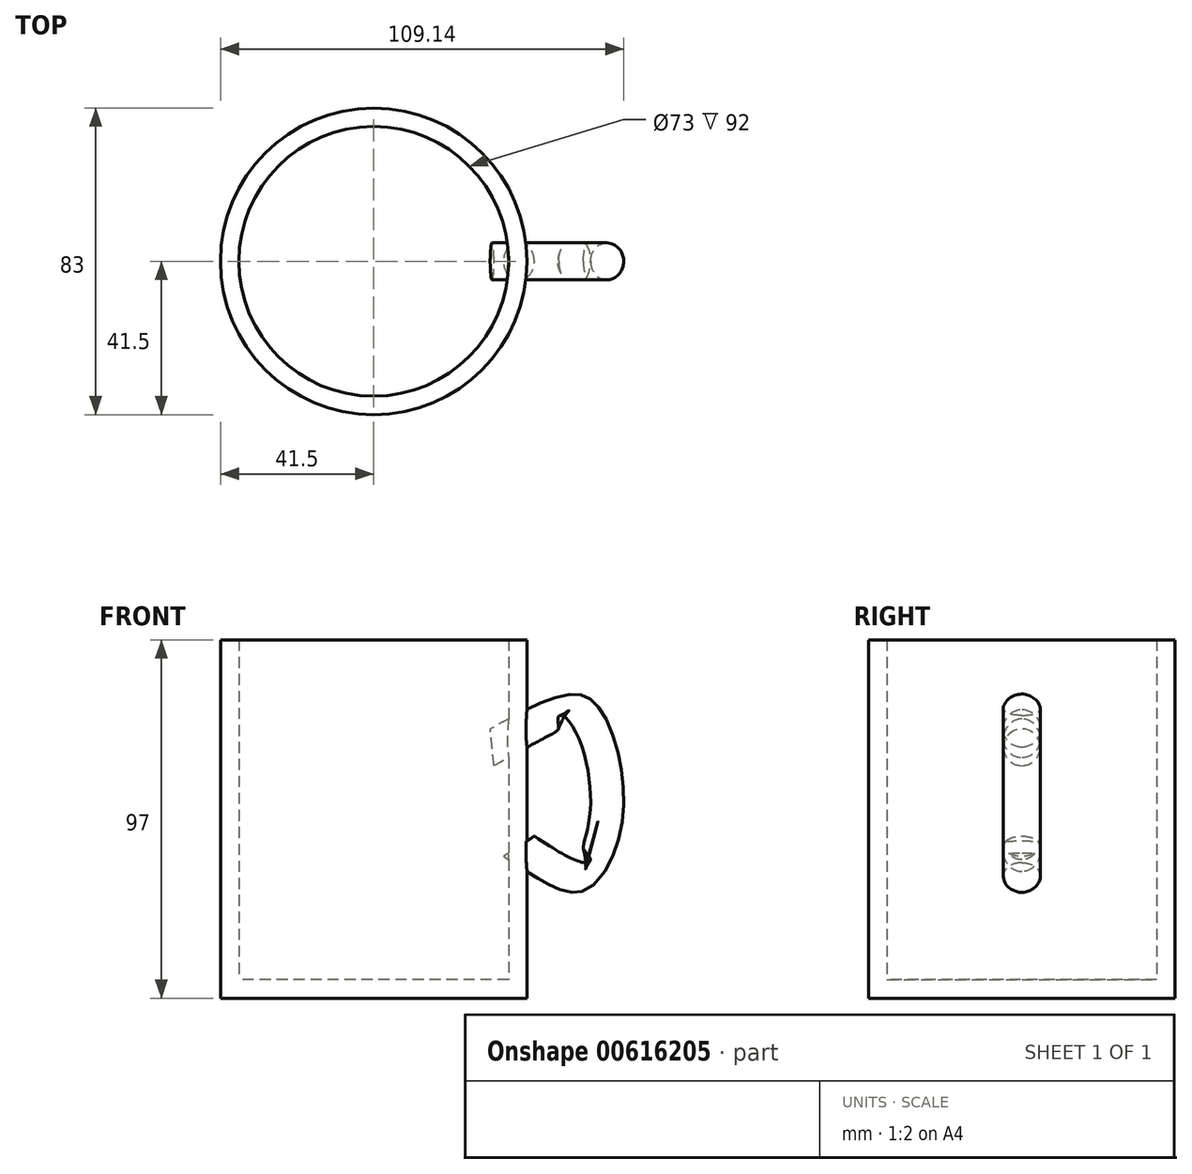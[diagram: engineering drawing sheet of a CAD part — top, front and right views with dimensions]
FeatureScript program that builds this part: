
annotation { "Feature Type Name" : "Feature", "Feature Type Description" : "" }
export const myFeature = defineFeature(function(context is Context, id is Id, definition is map)
    precondition{}
    {
        {
            var Q0;
            Q0=qCreatedBy(makeId("Top.planeOp"),FACE);
            var sketch = newSketch(context, id + "F0", { "sketchPlane" : qUnion([Q0])});
            skCircle(sketch, "E0", {"center": v(0, 0) * mm, "radius": 41.5 * mm});
            skSolve(sketch);
        }
        {
            var Q0;
            Q0 = qSketchRegion(id + "F0", true);
            extrude(context, id + "F1", {"entities" : qUnion([Q0]), "depth" : 97 * mm, "offsetDistance" : 25 * mm});
        }
        {
            var Q0;
            Q0=makeQuery(id+"F1.opExtrude","CAP_FACE",FACE,{"disambiguationData":[OSD([sQuery(id+"F0.wireOp",EDGE,"E0")])],"isStart":false});
            shell(context, id + "F2", {"entities" : qUnion([Q0]), "thickness" : 5 * mm});
        }
        {
            var Q0;
            Q0=qCreatedBy(makeId("Front.planeOp"),FACE);
            var sketch = newSketch(context, id + "F3", { "sketchPlane" : qUnion([Q0])});
            skFitSpline(sketch, "E1", {"points": [v(31.43, 73.65) * mm, v(60.97, 79.75) * mm, v(68.1, 49.2) * mm, v(57.91, 28.84) * mm, v(34.49, 38) * mm], "startDerivative": vector(209.07, 116.15) * mm, "endDerivative": vector(-152.62, 101.75) * mm});
            skSolve(sketch);
        }
        {
            var Q0;
            Q0=qCreatedBy(makeId("Right.planeOp"),FACE);
            cPlane(context, id + "F4", {"entities" : qUnion([Q0]), "cplaneType" : CPlaneType.OFFSET, "offset" : 45 * mm, "width" : 150 * mm, "height" : 150 * mm});
        }
        {
            var Q0;
            Q0=qCreatedBy(id+"F4.planeOp",FACE);
            var sketch = newSketch(context, id + "F5", { "sketchPlane" : qUnion([Q0])});
            skCircle(sketch, "E2", {"center": v(0, 74.8) * mm, "radius": 5 * mm});
            skSolve(sketch);
        }
        {
            var Q0;
            Q0 = qSketchRegion(id + "F5", true);
            var Q1;
            Q1 = qConstructionFilter(qBodyType(qCreatedBy(id + "F3" ,EDGE), BodyType.WIRE), ConstructionObject.NO);
            sweep(context, id + "F6", {"operationType" : NewBodyOperationType.ADD, "profiles" : qUnion([Q0]), "path" : qUnion([Q1])});
        }
    });
